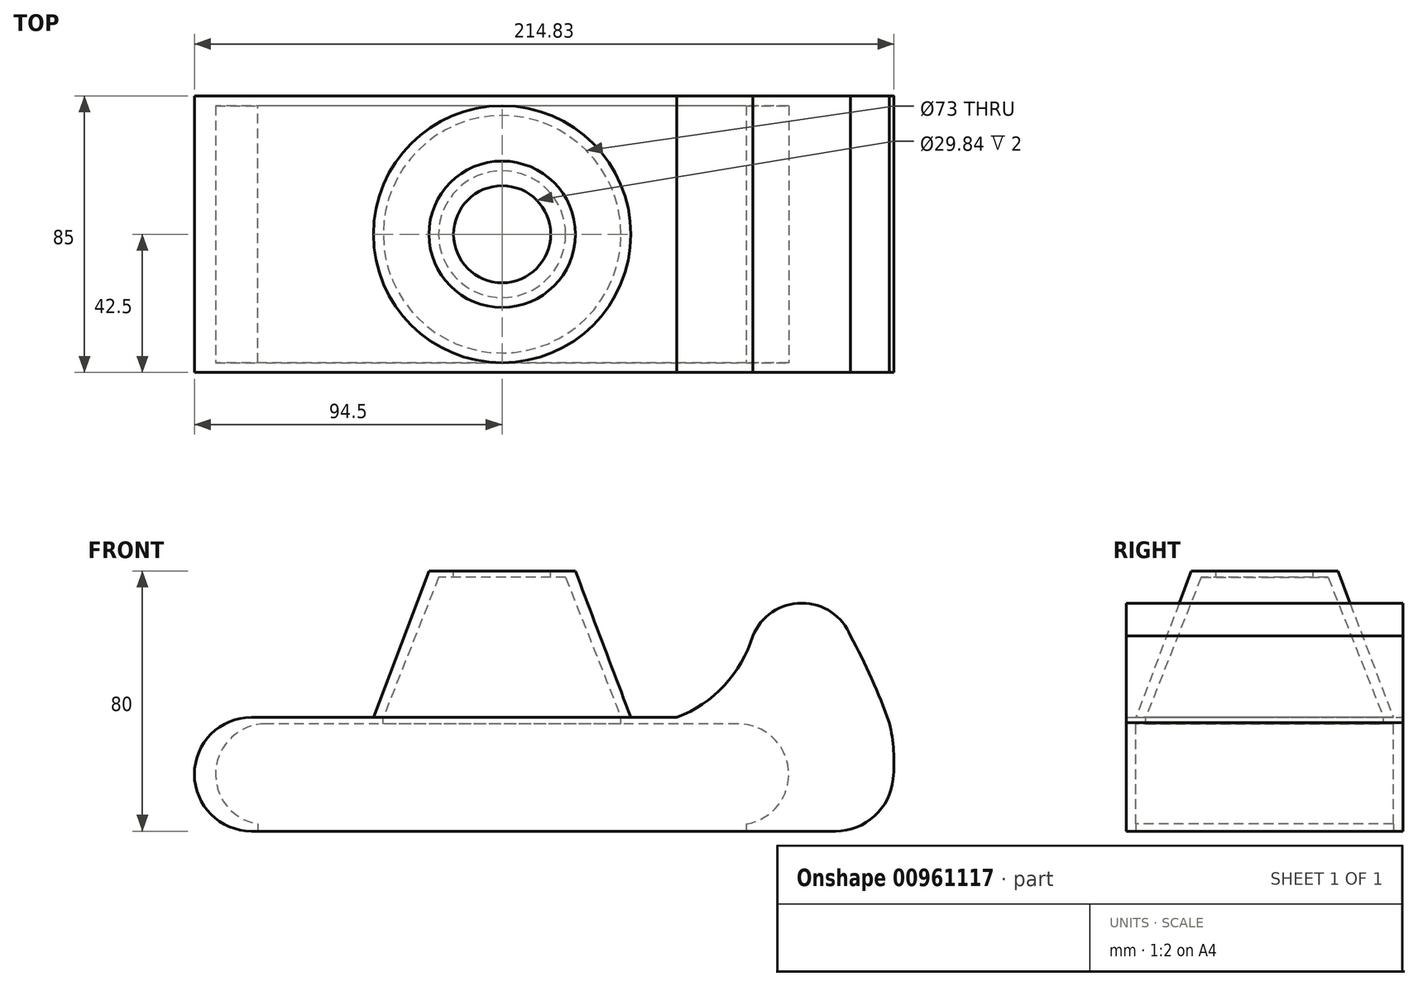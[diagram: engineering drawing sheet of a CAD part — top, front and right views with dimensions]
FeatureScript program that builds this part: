
annotation { "Feature Type Name" : "Feature", "Feature Type Description" : "" }
export const myFeature = defineFeature(function(context is Context, id is Id, definition is map)
    precondition{}
    {
        {
            var Q0;
            Q0=qCreatedBy(makeId("Front.planeOp"),FACE);
            var sketch = newSketch(context, id + "F0", { "sketchPlane" : qUnion([Q0])});
            skLineSegment(sketch, "E0.bottom", {"start": v(77, 17.5) * mm, "end": v(-77, 17.5) * mm, "construction": true});
            skLineSegment(sketch, "E0.top", {"start": v(77, -17.5) * mm, "end": v(-77, -17.5) * mm, "construction": true});
            skLineSegment(sketch, "E0.left", {"start": v(77, 17.5) * mm, "end": v(77, -17.5) * mm, "construction": true});
            skLineSegment(sketch, "E0.right", {"start": v(-77, 17.5) * mm, "end": v(-77, -17.5) * mm, "construction": true});
            skPoint(sketch, "E0.middle", {"position": v(0, 0) * mm});
            skArc(sketch, "E1", {"start": v(-77, 17.5) * mm, "mid": v(-94.5, 0) * mm, "end": v(-77, -17.5) * mm});
            skLineSegment(sketch, "E2", {"start": v(77, 17.5) * mm, "end": v(77, 42.5) * mm, "construction": true});
            skLineSegment(sketch, "E3", {"start": v(77, 42.5) * mm, "end": v(107, 42.5) * mm, "construction": true});
            skLineSegment(sketch, "E4", {"start": v(107, 42.5) * mm, "end": v(107, -17.5) * mm, "construction": true});
            skLineSegment(sketch, "E5", {"start": v(107, -17.5) * mm, "end": v(77, -17.5) * mm, "construction": true});
            skLineSegment(sketch, "E6.bottom", {"start": v(52.5, 0) * mm, "end": v(-52.5, 0) * mm, "construction": true});
            skLineSegment(sketch, "E6.top", {"start": v(52.5, 0) * mm, "end": v(-52.5, 0) * mm, "construction": true});
            skLineSegment(sketch, "E6.left", {"start": v(52.5, 0) * mm, "end": v(52.5, 0) * mm});
            skLineSegment(sketch, "E6.right", {"start": v(-52.5, 0) * mm, "end": v(-52.5, 0) * mm});
            skCircle(sketch, "E7", {"center": v(52.5, 0) * mm, "radius": 1.5 * mm, "construction": true});
            skCircle(sketch, "E8", {"center": v(-52.5, 0) * mm, "radius": 1.5 * mm, "construction": true});
            skLineSegment(sketch, "E9", {"start": v(107, 15.8) * mm, "end": v(118.94, 15.8) * mm, "construction": true});
            skArc(sketch, "E10", {"start": v(53.68, 17.5) * mm, "mid": v(68.22, 27.31) * mm, "end": v(77, 42.5) * mm});
            skArc(sketch, "E11", {"start": v(107, 42.5) * mm, "mid": v(92, 52.6) * mm, "end": v(77, 42.5) * mm});
            skArc(sketch, "E12", {"start": v(118.94, 15.8) * mm, "mid": v(113.49, 29.38) * mm, "end": v(107, 42.5) * mm});
            skArc(sketch, "E13", {"start": v(115.95, -17.5) * mm, "mid": v(120.12, -1.1) * mm, "end": v(118.94, 15.8) * mm});
            skLineSegment(sketch, "E14", {"start": v(115.95, -17.5) * mm, "end": v(107, -17.5) * mm});
            skLineSegment(sketch, "E15", {"start": v(53.68, 17.5) * mm, "end": v(-77, 17.5) * mm});
            skLineSegment(sketch, "E16", {"start": v(-77, -17.5) * mm, "end": v(107, -17.5) * mm});
            skSolve(sketch);
        }
        {
            var Q0;
            Q0 = qSketchRegion(id + "F0", true);
            extrude(context, id + "F1", {"entities" : qUnion([Q0]), "depth" : 85 * mm, "offsetDistance" : 25 * mm});
        }
        {
            var Q0;
            Q0=makeQuery(id+"F1.opExtrude","CAP_FACE",FACE,{"disambiguationData":[OSD([sQuery(id+"F0.wireOp",EDGE,"E1"),sQuery(id+"F0.wireOp",EDGE,"E10"),sQuery(id+"F0.wireOp",EDGE,"E11"),sQuery(id+"F0.wireOp",EDGE,"E12"),sQuery(id+"F0.wireOp",EDGE,"E13"),sQuery(id+"F0.wireOp",EDGE,"E14"),sQuery(id+"F0.wireOp",EDGE,"E15"),sQuery(id+"F0.wireOp",EDGE,"E16")])],"isStart":false});
            var sketch = newSketch(context, id + "F2", { "sketchPlane" : qUnion([Q0])});
            skLineSegment(sketch, "E17.bottom", {"start": v(72.5, 15.5) * mm, "end": v(-72.5, 15.5) * mm});
            skLineSegment(sketch, "E17.top", {"start": v(72.5, -15.5) * mm, "end": v(-72.5, -15.5) * mm});
            skLineSegment(sketch, "E17.left", {"start": v(72.5, 15.5) * mm, "end": v(72.5, -15.5) * mm});
            skLineSegment(sketch, "E17.right", {"start": v(-72.5, 15.5) * mm, "end": v(-72.5, -15.5) * mm});
            skPoint(sketch, "E17.middle", {"position": v(0, 0) * mm});
            skArc(sketch, "E18", {"start": v(-72.5, 15.5) * mm, "mid": v(-88, 0) * mm, "end": v(-72.5, -15.5) * mm});
            skArc(sketch, "E19", {"start": v(72.5, -15.5) * mm, "mid": v(88, 0) * mm, "end": v(72.5, 15.5) * mm});
            skSolve(sketch);
        }
        {
            var Q0;
            Q0 = qSketchRegion(id + "F2", true);
            extrude(context, id + "F3", {"entities" : qUnion([Q0]), "operationType" : NewBodyOperationType.REMOVE, "oppositeDirection" : true, "depth" : 82 * mm, "offsetDistance" : 25 * mm});
        }
        {
            var Q0;
            Q0=makeQuery(id+"F1.opExtrude","CAP_FACE",FACE,{"disambiguationData":[OSD([sQuery(id+"F0.wireOp",EDGE,"E1"),sQuery(id+"F0.wireOp",EDGE,"E10"),sQuery(id+"F0.wireOp",EDGE,"E11"),sQuery(id+"F0.wireOp",EDGE,"E12"),sQuery(id+"F0.wireOp",EDGE,"E13"),sQuery(id+"F0.wireOp",EDGE,"E14"),sQuery(id+"F0.wireOp",EDGE,"E15"),sQuery(id+"F0.wireOp",EDGE,"E16")])],"isStart":false});
            var sketch = newSketch(context, id + "F4", { "sketchPlane" : qUnion([Q0])});
            skLineSegment(sketch, "E20", {"start": v(-89.82, 7.1) * mm, "end": v(-80.33, 15.81) * mm});
            skLineSegment(sketch, "E21", {"start": v(-80.33, 15.81) * mm, "end": v(-69.61, 16.64) * mm});
            skLineSegment(sketch, "E22", {"start": v(-69.61, 16.64) * mm, "end": v(67.79, 16.64) * mm});
            skLineSegment(sketch, "E23", {"start": v(67.79, 16.64) * mm, "end": v(83.17, 16.64) * mm});
            skLineSegment(sketch, "E24", {"start": v(83.17, 16.64) * mm, "end": v(95.83, 5.41) * mm});
            skLineSegment(sketch, "E25", {"start": v(95.83, 5.41) * mm, "end": v(93.18, -10.93) * mm});
            skLineSegment(sketch, "E26", {"start": v(93.18, -10.93) * mm, "end": v(83.17, -15.5) * mm});
            skLineSegment(sketch, "E27", {"start": v(83.17, -15.5) * mm, "end": v(74.39, -16.42) * mm});
            skLineSegment(sketch, "E28", {"start": v(74.39, -16.42) * mm, "end": v(-77, -16.42) * mm});
            skLineSegment(sketch, "E29", {"start": v(-77, -16.42) * mm, "end": v(-85, -14.22) * mm});
            skLineSegment(sketch, "E30", {"start": v(-85, -14.22) * mm, "end": v(-88.28, -7.94) * mm});
            skLineSegment(sketch, "E31", {"start": v(-88.28, -7.94) * mm, "end": v(-91.01, 2.98) * mm});
            skLineSegment(sketch, "E32", {"start": v(-91.01, 2.98) * mm, "end": v(-89.82, 7.1) * mm});
            skSolve(sketch);
        }
        {
            var Q0;
            Q0 = qSketchRegion(id + "F4", true);
            extrude(context, id + "F5", {"entities" : qUnion([Q0]), "operationType" : NewBodyOperationType.ADD, "oppositeDirection" : true, "depth" : 3 * mm, "offsetDistance" : 25 * mm});
        }
        {
            var Q0;
            Q0=makeQuery(id+"F1.opExtrude","SWEPT_FACE",FACE,{"disambiguationData":[OSD([sQuery(id+"F0.wireOp",EDGE,"E15")])]});
            var sketch = newSketch(context, id + "F6", { "sketchPlane" : qUnion([Q0])});
            skLineSegment(sketch, "E33", {"start": v(0, 0) * mm, "end": v(0, -85) * mm, "construction": true});
            skCircle(sketch, "E34", {"center": v(0, -42.5) * mm, "radius": 36.5 * mm});
            skSolve(sketch);
        }
        {
            var Q0;
            Q0 = qSketchRegion(id + "F6", true);
            extrude(context, id + "F7", {"entities" : qUnion([Q0]), "operationType" : NewBodyOperationType.REMOVE, "oppositeDirection" : true, "depth" : 25 * mm, "offsetDistance" : 25 * mm});
        }
        {
            var Q0;
            Q0=makeQuery(id+"F1.opExtrude","SWEPT_FACE",FACE,{"disambiguationData":[OSD([sQuery(id+"F0.wireOp",EDGE,"E14"),sQuery(id+"F0.wireOp",EDGE,"E16")])]});
            var sketch = newSketch(context, id + "F8", { "sketchPlane" : qUnion([Q0])});
            skLineSegment(sketch, "E35", {"start": v(0, 0) * mm, "end": v(0, 85) * mm, "construction": true});
            skLineSegment(sketch, "E36.bottom", {"start": v(75, 82) * mm, "end": v(-75, 82) * mm});
            skLineSegment(sketch, "E36.top", {"start": v(75, 3) * mm, "end": v(-75, 3) * mm});
            skLineSegment(sketch, "E36.left", {"start": v(75, 82) * mm, "end": v(75, 3) * mm});
            skLineSegment(sketch, "E36.right", {"start": v(-75, 82) * mm, "end": v(-75, 3) * mm});
            skPoint(sketch, "E36.middle", {"position": v(0, 42.5) * mm});
            skSolve(sketch);
        }
        {
            var Q0;
            Q0 = qSketchRegion(id + "F8", true);
            extrude(context, id + "F9", {"entities" : qUnion([Q0]), "operationType" : NewBodyOperationType.REMOVE, "oppositeDirection" : true, "depth" : 25 * mm, "offsetDistance" : 25 * mm});
        }
        {
            var Q0;
            Q0=makeQuery(id+"F1.opExtrude","SWEPT_FACE",FACE,{"disambiguationData":[OSD([sQuery(id+"F0.wireOp",EDGE,"E15")])]});
            cPlane(context, id + "F10", {"entities" : qUnion([Q0]), "cplaneType" : CPlaneType.OFFSET, "offset" : 45 * mm, "width" : 150 * mm, "height" : 150 * mm});
        }
        {
            var Q0;
            Q0=qCreatedBy(id+"F10.planeOp",FACE);
            var sketch = newSketch(context, id + "F11", { "sketchPlane" : qUnion([Q0])});
            skLineSegment(sketch, "E37", {"start": v(0, 0) * mm, "end": v(0, -85) * mm, "construction": true});
            skCircle(sketch, "E38", {"center": v(0, -42.5) * mm, "radius": 22.5 * mm});
            skSolve(sketch);
        }
        {
            var Q0;
            Q0=makeQuery(id+"F1.opExtrude","SWEPT_FACE",FACE,{"disambiguationData":[OSD([sQuery(id+"F0.wireOp",EDGE,"E15")])]});
            var sketch = newSketch(context, id + "F12", { "sketchPlane" : qUnion([Q0])});
            skLineSegment(sketch, "E39", {"start": v(0, 0) * mm, "end": v(0, -85) * mm, "construction": true});
            skCircle(sketch, "E40", {"center": v(0, -42.5) * mm, "radius": 39.5 * mm});
            skSolve(sketch);
        }
        {
            var Q1;
            Q1 = qSketchRegion(id + "F12", true);
            var Q2;
            Q2 = qSketchRegion(id + "F11", true);
            loft(context, id + "F13", {"operationType" : NewBodyOperationType.ADD, "sheetProfilesArray" : [{ "sheetProfileEntities" : qUnion([Q1]) }, { "sheetProfileEntities" : qUnion([Q2]) }]});
        }
        {
            var Q0;
            Q0=qCreatedBy(id+"F10.planeOp",FACE);
            cPlane(context, id + "F14", {"entities" : qUnion([Q0]), "cplaneType" : CPlaneType.OFFSET, "offset" : 2 * mm, "oppositeDirection" : true, "width" : 150 * mm, "height" : 150 * mm});
        }
        {
            var Q0;
            Q0=qCreatedBy(id+"F14.planeOp",FACE);
            var sketch = newSketch(context, id + "F15", { "sketchPlane" : qUnion([Q0])});
            skLineSegment(sketch, "E41", {"start": v(0, 0) * mm, "end": v(0, -85) * mm, "construction": true});
            skCircle(sketch, "E42", {"center": v(0, -42.5) * mm, "radius": 19.5 * mm});
            skSolve(sketch);
        }
        {
            var Q0;
            {var subQ0=makeQuery(id+"F12.imprint","IMPRINT",EDGE,{"derivedFrom":makeQuery(id+"F7.boolean.opBoolean","COPY",EDGE,{"derivedFrom":makeQuery(id+"F7.opExtrude","CAP_EDGE",EDGE,{"disambiguationData":[OSD([sQuery(id+"F6.wireOp",EDGE,"E34")])],"isStart":true})})});Q0=makeQuery(id+"F13.opLoft","CAP_FACE",FACE,{"disambiguationData":[OSD([makeQuery(id+"F12.imprint","IMPRINT",FACE,{"disambiguationData":[TD([[subQ0,1.0]])]}),makeQuery(id+"F12.imprint","IMPRINT",FACE,{"disambiguationData":[TD([[makeQuery(id+"F12.imprint","IMPRINT",EDGE,{"derivedFrom":sQuery(id+"F12.wireOp",EDGE,"E40")}),1.0]])]})])],"isStart":true});}
            var sketch = newSketch(context, id + "F16", { "sketchPlane" : qUnion([Q0])});
            skCircle(sketch, "E43", {"center": v(0, 42.5) * mm, "radius": 36.5 * mm});
            skSolve(sketch);
        }
        {
            var Q1;
            Q1 = qSketchRegion(id + "F15", true);
            var Q2;
            Q2 = qSketchRegion(id + "F16", true);
            loft(context, id + "F17", {"operationType" : NewBodyOperationType.REMOVE, "sheetProfilesArray" : [{ "sheetProfileEntities" : qUnion([Q1]) }, { "sheetProfileEntities" : qUnion([Q2]) }]});
        }
        {
            var Q0;
            Q0=makeQuery(id+"F13.opLoft","CAP_FACE",FACE,{"disambiguationData":[OSD([makeQuery(id+"F11.imprint","IMPRINT",FACE,{"disambiguationData":[TD([[makeQuery(id+"F11.imprint","IMPRINT",EDGE,{"derivedFrom":sQuery(id+"F11.wireOp",EDGE,"E38")}),1.0]])]})])],"isStart":true});
            var sketch = newSketch(context, id + "F18", { "sketchPlane" : qUnion([Q0])});
            skCircle(sketch, "E44", {"center": v(0, -42.5) * mm, "radius": 14.92 * mm});
            skSolve(sketch);
        }
        {
            var Q0;
            Q0 = qSketchRegion(id + "F18", true);
            extrude(context, id + "F19", {"entities" : qUnion([Q0]), "operationType" : NewBodyOperationType.REMOVE, "oppositeDirection" : true, "depth" : 25 * mm, "offsetDistance" : 25 * mm});
        }
        {
            var Q0;
            Q0=makeQuery(id+"F1.opExtrude","SWEPT_EDGE",EDGE,{"disambiguationData":[OSD([sQuery(id+"F0.wireOp",EDGE,"E13"),sQuery(id+"F0.wireOp",EDGE,"E14")])]});
            fillet(context, id + "F20", {"entities" : qUnion([Q0]), "radius" : 17.8 * mm, "tangentPropagation" : true, "allowEdgeOverflow" : false});
        }
    });
